# Revit family: Telephone_Wall
name_source: partatom
category: Telephone Devices
units: mm (PartAtom-declared; Revit-internal decimal feet)

## family parameters
Always vertical = Yes
Classification Number = 23.85.50.17
Cut with Voids When Loaded = No
Maintain Annotation Orientation = No
Part Type = Normal
Room Calculation Point = No
Round Connector Dimension = Use Diameter
Shared = No
Work Plane-Based = No

## types (2) — shared parameters
Accent Color = Plastic - ABS, Silver
Assembly Code = E1010800
Buttons = Plastic - ABS, White
Connections = (1) - RJ-11
Connectivity = Telecom, PBX, Intercom
Construction Details = http://www.arcat.com
Default Elevation = 0' - 0"
Description = Desk Telephone
Expected Lifespan (Years) = 10
Green Building - LEED = http://www.arcat.com
Keynote = 16720
Lines = 1
Manufacturer = Generic
Manufacturer Fax = (203) 939-2444
Manufacturer Website = http://www.arcat.com
Model = Generic
Product Data = http://www.arcat.com
Product Properties = http://www.arcat.com
Specification = http://www.arcat.com
Warranty Duration (Years) = 1
zero-valued in all types: Maintenance Schedule (Months)

## per-type parameters (varying)
| type | Body and Handset Material | Cord Material |
| Residential | Plastic - ABS, Yellow | Plastic - ABS, Yellow |
| Emergency | Plastic - ABS, Red | Plastic - HDPE, Black |

## geometry (parser evidence)
native form markers: Sweep x3
no freeform markers — native parametric forms only
